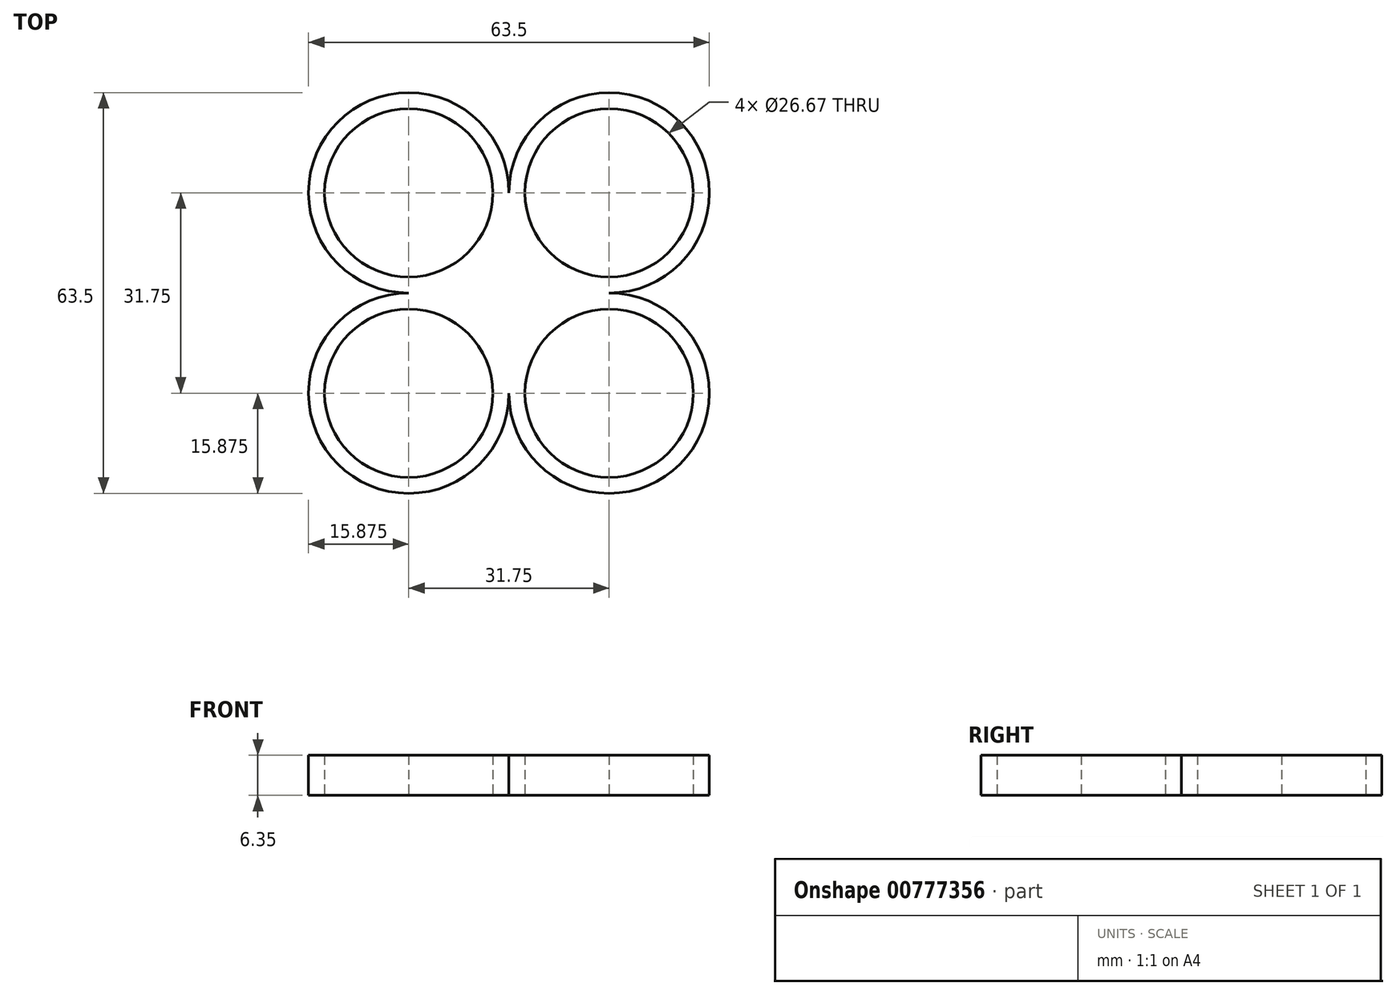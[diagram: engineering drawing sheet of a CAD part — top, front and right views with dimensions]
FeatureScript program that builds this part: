
annotation { "Feature Type Name" : "Feature", "Feature Type Description" : "" }
export const myFeature = defineFeature(function(context is Context, id is Id, definition is map)
    precondition{}
    {
        {
            var Q0;
            Q0=qCreatedBy(makeId("Top.planeOp"),FACE);
            var sketch = newSketch(context, id + "F0", { "sketchPlane" : qUnion([Q0])});
            skCircle(sketch, "E0", {"center": v(-15.88, 15.88) * mm, "radius": 13.34 * mm});
            skArc(sketch, "E1", {"start": v(0, 15.88) * mm, "mid": v(-27.1, 27.1) * mm, "end": v(-15.88, 0) * mm});
            skLineSegment(sketch, "E2", {"start": v(-15.88, 0) * mm, "end": v(0, 0) * mm});
            skLineSegment(sketch, "E3", {"start": v(0, 0) * mm, "end": v(0, 15.88) * mm});
            skSolve(sketch);
        }
        {
            var Q0;
            Q0 = qSketchRegion(id + "F0", true);
            extrude(context, id + "F1", {"entities" : qUnion([Q0]), "depth" : 6.35 * mm, "offsetDistance" : 25.4 * mm});
        }
        {
            var Q0;
            Q0=makeQuery(id+"F1.opExtrude","SWEPT_BODY",BODY,{"disambiguationData":[OSD([sQuery(id+"F0.wireOp",EDGE,"E0"),sQuery(id+"F0.wireOp",EDGE,"E1"),sQuery(id+"F0.wireOp",EDGE,"E2"),sQuery(id+"F0.wireOp",EDGE,"E3")])]});
            var Q1;
            Q1=qCreatedBy(makeId("Right.planeOp"),FACE);
            mirror(context, id + "F2", {"operationType" : NewBodyOperationType.ADD, "entities" : qUnion([Q0]), "mirrorPlane" : qUnion([Q1])});
        }
        {
            var Q0;
            Q0=makeQuery(id+"F1.opExtrude","SWEPT_BODY",BODY,{"disambiguationData":[OSD([sQuery(id+"F0.wireOp",EDGE,"E0"),sQuery(id+"F0.wireOp",EDGE,"E1"),sQuery(id+"F0.wireOp",EDGE,"E2"),sQuery(id+"F0.wireOp",EDGE,"E3")])]});
            var Q1;
            Q1=qCreatedBy(makeId("Front.planeOp"),FACE);
            mirror(context, id + "F3", {"operationType" : NewBodyOperationType.ADD, "entities" : qUnion([Q0]), "mirrorPlane" : qUnion([Q1])});
        }
    });
